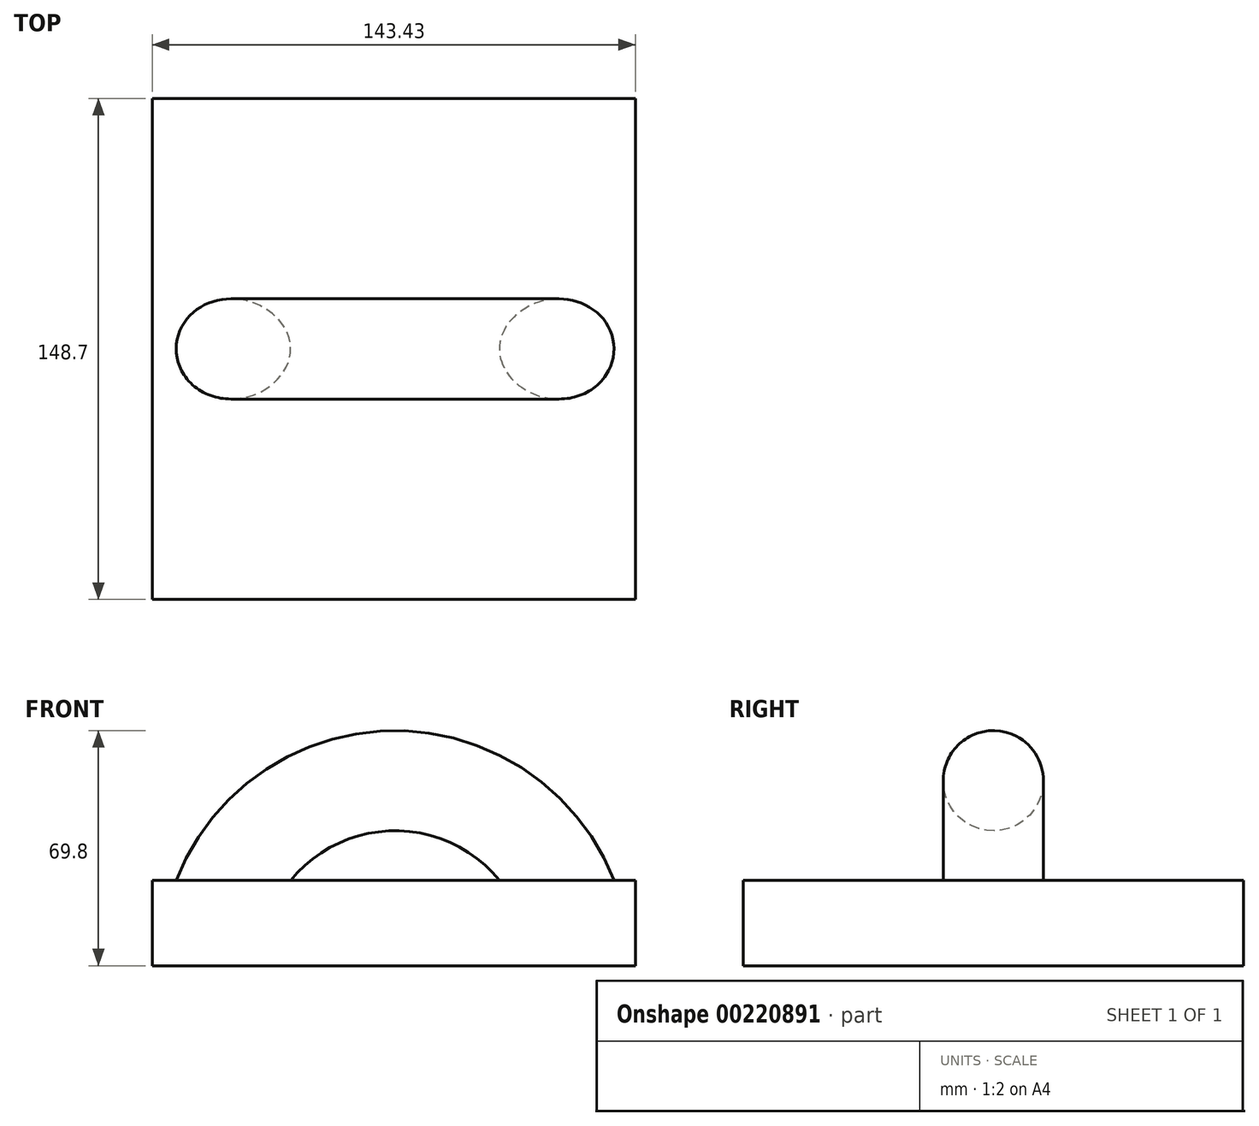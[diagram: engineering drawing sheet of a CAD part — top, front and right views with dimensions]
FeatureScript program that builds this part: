
annotation { "Feature Type Name" : "Feature", "Feature Type Description" : "" }
export const myFeature = defineFeature(function(context is Context, id is Id, definition is map)
    precondition{}
    {
        {
            var Q0;
            Q0=qCreatedBy(makeId("Top.planeOp"),FACE);
            var sketch = newSketch(context, id + "F0", { "sketchPlane" : qUnion([Q0])});
            skLineSegment(sketch, "E0.bottom", {"start": v(-72.25, 74.35) * mm, "end": v(-0.18, 74.35) * mm});
            skLineSegment(sketch, "E0.top", {"start": v(-72.25, -74.35) * mm, "end": v(-0.18, -74.35) * mm});
            skLineSegment(sketch, "E0.left", {"start": v(-72.25, 74.35) * mm, "end": v(-72.25, -74.35) * mm});
            skLineSegment(sketch, "E0.right", {"start": v(-0.18, 74.35) * mm, "end": v(-0.18, -74.35) * mm});
            skPoint(sketch, "E0.middle", {"position": v(-36.21, 0) * mm});
            skLineSegment(sketch, "E1.bottom", {"start": v(-0.18, 74.35) * mm, "end": v(71.18, 74.35) * mm});
            skLineSegment(sketch, "E1.top", {"start": v(-0.18, -74.35) * mm, "end": v(71.18, -74.35) * mm});
            skLineSegment(sketch, "E1.right", {"start": v(71.18, 74.35) * mm, "end": v(71.18, -74.35) * mm});
            skPoint(sketch, "E1.middle", {"position": v(35.5, 0) * mm});
            skSolve(sketch);
        }
        {
            var Q0;
            Q0=makeQuery(id+"F0.imprint","IMPRINT",FACE,{"disambiguationData":[TD([[makeQuery(id+"F0.imprint","IMPRINT",EDGE,{"derivedFrom":sQuery(id+"F0.wireOp",EDGE,"E1.bottom")}),-1.0]])]});
            var sketch = newSketch(context, id + "F1", { "sketchPlane" : qUnion([Q0])});
            skCircle(sketch, "E2", {"center": v(54.76, 0) * mm, "radius": 14.87 * mm});
            skSolve(sketch);
        }
        {
            var Q0;
            Q0=makeQuery(id+"F1.imprint","IMPRINT",FACE,{"disambiguationData":[TD([[makeQuery(id+"F1.imprint","IMPRINT",EDGE,{"derivedFrom":sQuery(id+"F1.wireOp",EDGE,"E2")}),1.0]])]});
            var Q1;
            Q1=sQuery(id+"F0.wireOp",EDGE,"E0.right");
            revolve(context, id + "F2", {"entities" : qUnion([Q0]), "axis" : qUnion([Q1]), "revolveType" : RevolveType.ONE_DIRECTION, "angle" : 180 * degree});
        }
        {
            var Q0;
            Q0 = qSketchRegion(id + "F0", true);
            extrude(context, id + "F3", {"entities" : qUnion([Q0]), "operationType" : NewBodyOperationType.ADD, "depth" : 25.4 * mm});
        }
    });
